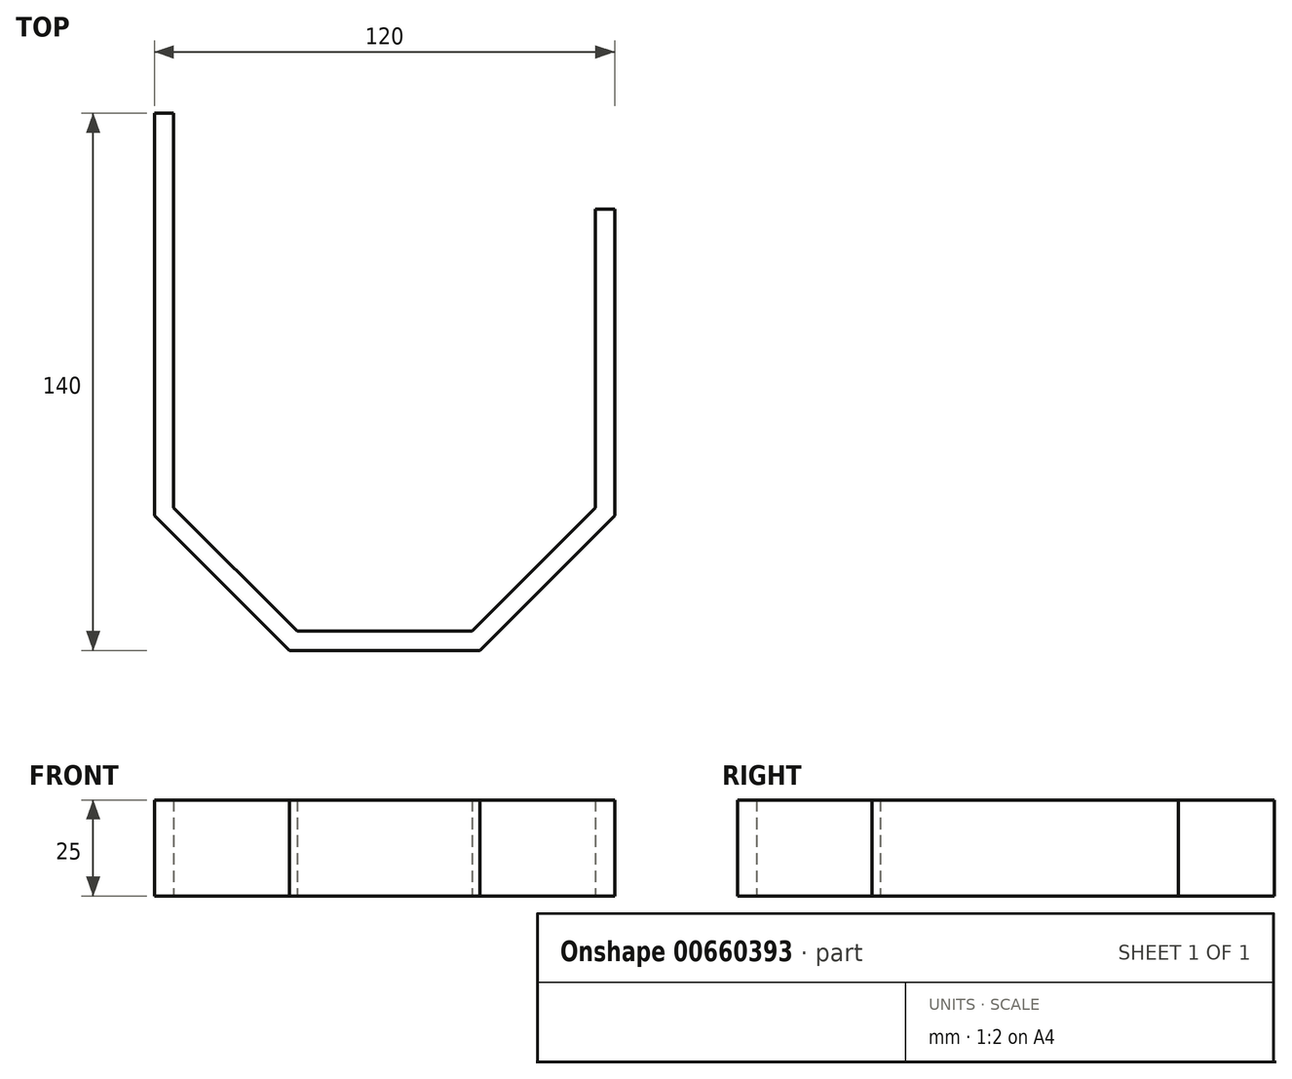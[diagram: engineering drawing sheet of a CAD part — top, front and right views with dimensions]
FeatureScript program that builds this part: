
annotation { "Feature Type Name" : "Feature", "Feature Type Description" : "" }
export const myFeature = defineFeature(function(context is Context, id is Id, definition is map)
    precondition{}
    {
        {
            var Q0;
            Q0=qCreatedBy(makeId("Top.planeOp"),FACE);
            var sketch = newSketch(context, id + "F0", { "sketchPlane" : qUnion([Q0])});
            skCircle(sketch, "E0", {"center": v(0, 0) * mm, "radius": 50 * mm, "construction": true});
            skCircle(sketch, "E1", {"center": v(0, 0) * mm, "radius": 55 * mm, "construction": true});
            skLineSegment(sketch, "E2", {"start": v(-55, 55) * mm, "end": v(-55, -22.78) * mm});
            skLineSegment(sketch, "E3", {"start": v(-55, -22.78) * mm, "end": v(-22.78, -55) * mm});
            skLineSegment(sketch, "E4", {"start": v(-22.78, -55) * mm, "end": v(22.78, -55) * mm});
            skLineSegment(sketch, "E5", {"start": v(22.78, -55) * mm, "end": v(55, -22.78) * mm});
            skLineSegment(sketch, "E6", {"start": v(55, -22.78) * mm, "end": v(55, 55) * mm});
            skLineSegment(sketch, "E7", {"start": v(-55, 55) * mm, "end": v(55, 55) * mm, "construction": true});
            skLineSegment(sketch, "E8.0", {"start": v(60, -24.85) * mm, "end": v(60, 55) * mm});
            skLineSegment(sketch, "E8.1", {"start": v(-60, 55) * mm, "end": v(-60, -24.85) * mm});
            skLineSegment(sketch, "E8.2", {"start": v(-60, -24.85) * mm, "end": v(-24.85, -60) * mm});
            skLineSegment(sketch, "E8.3", {"start": v(-24.85, -60) * mm, "end": v(24.85, -60) * mm});
            skLineSegment(sketch, "E8.4", {"start": v(24.85, -60) * mm, "end": v(60, -24.85) * mm});
            skLineSegment(sketch, "E9", {"start": v(55, 55) * mm, "end": v(60, 55) * mm});
            skLineSegment(sketch, "E10.top", {"start": v(-60, 80) * mm, "end": v(-55, 80) * mm});
            skLineSegment(sketch, "E10.left", {"start": v(-60, 55) * mm, "end": v(-60, 80) * mm});
            skLineSegment(sketch, "E10.right", {"start": v(-55, 55) * mm, "end": v(-55, 80) * mm});
            skLineSegment(sketch, "E11", {"start": v(-55, 55) * mm, "end": v(-60, 55) * mm, "construction": true});
            skSolve(sketch);
        }
        {
            var Q0;
            Q0=makeQuery(id+"F0.imprint","IMPRINT",FACE,{"disambiguationData":[TD([[makeQuery(id+"F0.imprint","IMPRINT",EDGE,{"derivedFrom":sQuery(id+"F0.wireOp",EDGE,"E2")}),-1.0]])]});
            extrude(context, id + "F1", {"entities" : qUnion([Q0]), "depth" : 25 * mm, "offsetDistance" : 25 * mm});
        }
    });
